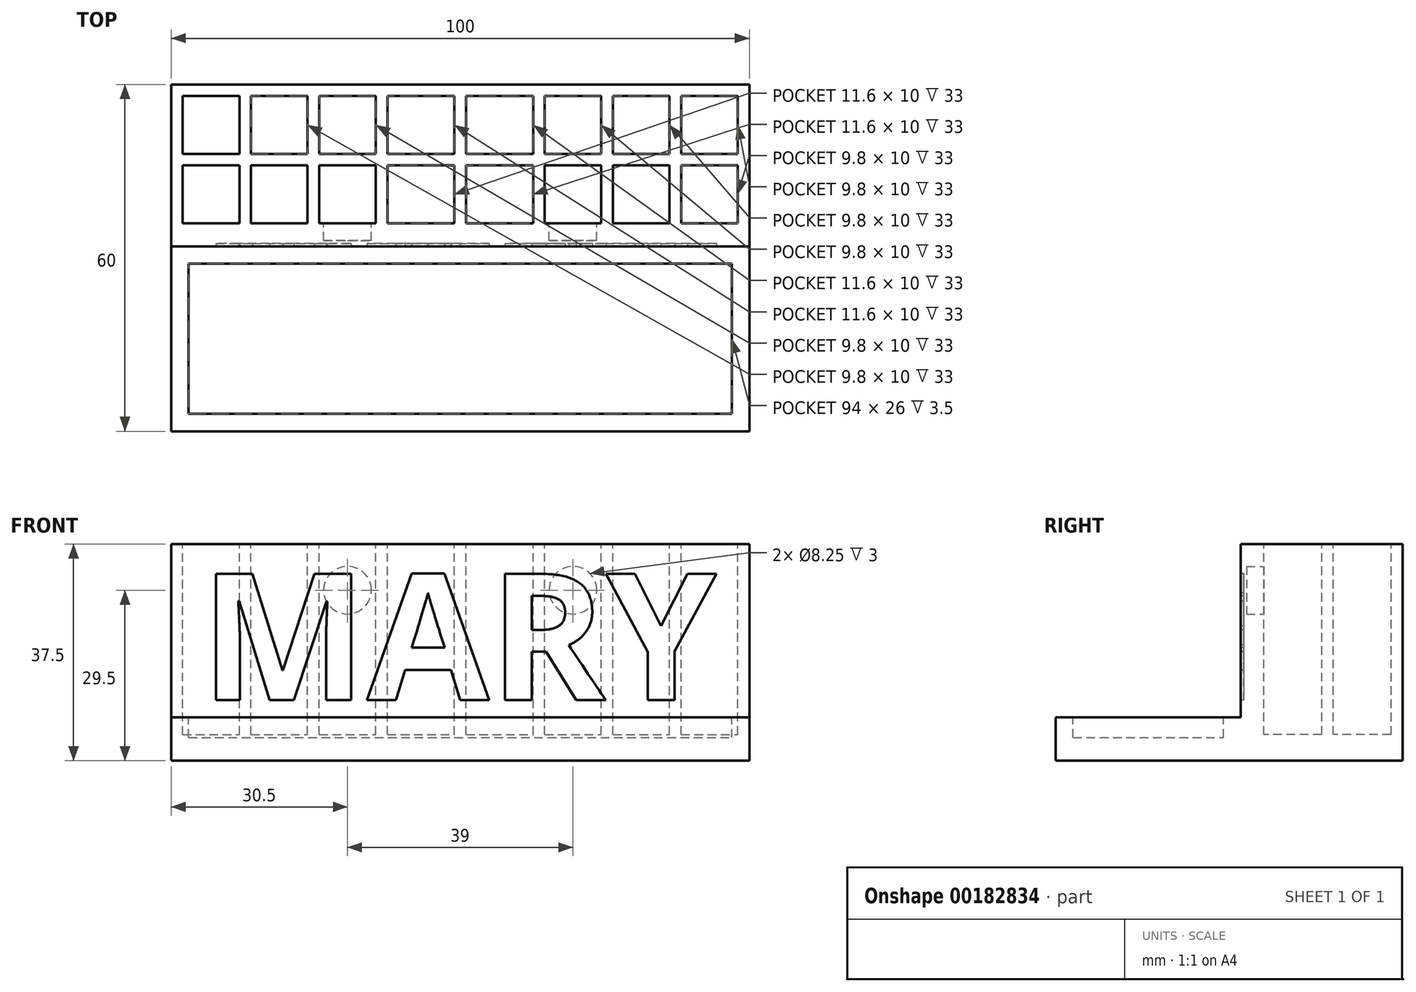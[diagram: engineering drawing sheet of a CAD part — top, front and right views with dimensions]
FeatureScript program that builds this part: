
annotation { "Feature Type Name" : "Feature", "Feature Type Description" : "" }
export const myFeature = defineFeature(function(context is Context, id is Id, definition is map)
    precondition{}
    {
        {
            var Q0;
            Q0=qCreatedBy(makeId("Top.planeOp"),FACE);
            var sketch = newSketch(context, id + "F0", { "sketchPlane" : qUnion([Q0])});
            skLineSegment(sketch, "E0.bottom", {"start": v(-50, 30) * mm, "end": v(50, 30) * mm});
            skLineSegment(sketch, "E0.top", {"start": v(-50, -30) * mm, "end": v(50, -30) * mm});
            skLineSegment(sketch, "E0.left", {"start": v(-50, 30) * mm, "end": v(-50, -30) * mm});
            skLineSegment(sketch, "E0.right", {"start": v(50, 30) * mm, "end": v(50, -30) * mm});
            skSolve(sketch);
        }
        {
            var Q0;
            Q0 = qSketchRegion(id + "F0", true);
            extrude(context, id + "F1", {"entities" : qUnion([Q0]), "depth" : 7.5 * mm});
        }
        {
            var Q0;
            Q0=makeQuery(id+"F1.opExtrude","CAP_FACE",FACE,{"disambiguationData":[OSD([sQuery(id+"F0.wireOp",EDGE,"E0.bottom"),sQuery(id+"F0.wireOp",EDGE,"E0.top"),sQuery(id+"F0.wireOp",EDGE,"E0.left"),sQuery(id+"F0.wireOp",EDGE,"E0.right")])],"isStart":false});
            var sketch = newSketch(context, id + "F2", { "sketchPlane" : qUnion([Q0])});
            skLineSegment(sketch, "E1.bottom", {"start": v(-50, 30) * mm, "end": v(50, 30) * mm});
            skLineSegment(sketch, "E1.top", {"start": v(-50, 2) * mm, "end": v(50, 2) * mm});
            skLineSegment(sketch, "E1.left", {"start": v(-50, 30) * mm, "end": v(-50, 2) * mm});
            skLineSegment(sketch, "E1.right", {"start": v(50, 30) * mm, "end": v(50, 2) * mm});
            skSolve(sketch);
        }
        {
            var Q0;
            Q0 = qSketchRegion(id + "F2", true);
            extrude(context, id + "F3", {"entities" : qUnion([Q0]), "operationType" : NewBodyOperationType.ADD, "depth" : 30 * mm});
        }
        {
            var Q0;
            Q0=makeQuery(id+"F3.opExtrude","CAP_FACE",FACE,{"disambiguationData":[OSD([sQuery(id+"F2.wireOp",EDGE,"E1.bottom"),sQuery(id+"F2.wireOp",EDGE,"E1.top"),sQuery(id+"F2.wireOp",EDGE,"E1.left"),sQuery(id+"F2.wireOp",EDGE,"E1.right")])],"isStart":false});
            var sketch = newSketch(context, id + "F4", { "sketchPlane" : qUnion([Q0])});
            skLineSegment(sketch, "E2.bottom", {"start": v(-48, 28) * mm, "end": v(48, 28) * mm});
            skLineSegment(sketch, "E2.top", {"start": v(-48, 6) * mm, "end": v(48, 6) * mm});
            skLineSegment(sketch, "E2.left", {"start": v(-48, 28) * mm, "end": v(-48, 6) * mm});
            skLineSegment(sketch, "E2.right", {"start": v(48, 28) * mm, "end": v(48, 6) * mm});
            skLineSegment(sketch, "E3.bottom", {"start": v(-48, 18) * mm, "end": v(48, 18) * mm});
            skLineSegment(sketch, "E3.top", {"start": v(-48, 16) * mm, "end": v(48, 16) * mm});
            skLineSegment(sketch, "E3.left", {"start": v(-48, 18) * mm, "end": v(-48, 16) * mm});
            skLineSegment(sketch, "E3.right", {"start": v(48, 18) * mm, "end": v(48, 16) * mm});
            skLineSegment(sketch, "E4.bottom", {"start": v(-38.2, 28) * mm, "end": v(-36.2, 28) * mm});
            skLineSegment(sketch, "E4.top", {"start": v(-38.2, 6) * mm, "end": v(-36.2, 6) * mm});
            skLineSegment(sketch, "E4.left", {"start": v(-38.2, 28) * mm, "end": v(-38.2, 6) * mm});
            skLineSegment(sketch, "E4.right", {"start": v(-36.2, 28) * mm, "end": v(-36.2, 6) * mm});
            skLineSegment(sketch, "E5.bottom", {"start": v(38.2, 28) * mm, "end": v(36.2, 28) * mm});
            skLineSegment(sketch, "E5.top", {"start": v(38.2, 6) * mm, "end": v(36.2, 6) * mm});
            skLineSegment(sketch, "E5.left", {"start": v(38.2, 28) * mm, "end": v(38.2, 6) * mm});
            skLineSegment(sketch, "E5.right", {"start": v(36.2, 28) * mm, "end": v(36.2, 6) * mm});
            skLineSegment(sketch, "E6.bottom", {"start": v(26.4, 28) * mm, "end": v(24.4, 28) * mm});
            skLineSegment(sketch, "E6.top", {"start": v(26.4, 6) * mm, "end": v(24.4, 6) * mm});
            skLineSegment(sketch, "E6.left", {"start": v(26.4, 28) * mm, "end": v(26.4, 6) * mm});
            skLineSegment(sketch, "E6.right", {"start": v(24.4, 28) * mm, "end": v(24.4, 6) * mm});
            skLineSegment(sketch, "E7.bottom", {"start": v(-26.4, 28) * mm, "end": v(-24.4, 28) * mm});
            skLineSegment(sketch, "E7.top", {"start": v(-26.4, 6) * mm, "end": v(-24.4, 6) * mm});
            skLineSegment(sketch, "E7.left", {"start": v(-26.4, 28) * mm, "end": v(-26.4, 6) * mm});
            skLineSegment(sketch, "E7.right", {"start": v(-24.4, 28) * mm, "end": v(-24.4, 6) * mm});
            skLineSegment(sketch, "E8.bottom", {"start": v(14.6, 28) * mm, "end": v(12.6, 28) * mm});
            skLineSegment(sketch, "E8.top", {"start": v(14.6, 6) * mm, "end": v(12.6, 6) * mm});
            skLineSegment(sketch, "E8.left", {"start": v(14.6, 28) * mm, "end": v(14.6, 6) * mm});
            skLineSegment(sketch, "E8.right", {"start": v(12.6, 28) * mm, "end": v(12.6, 6) * mm});
            skLineSegment(sketch, "E9.bottom", {"start": v(-14.6, 28) * mm, "end": v(-12.6, 28) * mm});
            skLineSegment(sketch, "E9.top", {"start": v(-14.6, 6) * mm, "end": v(-12.6, 6) * mm});
            skLineSegment(sketch, "E9.left", {"start": v(-14.6, 28) * mm, "end": v(-14.6, 6) * mm});
            skLineSegment(sketch, "E9.right", {"start": v(-12.6, 28) * mm, "end": v(-12.6, 6) * mm});
            skLineSegment(sketch, "E10.bottom", {"start": v(-1, 28) * mm, "end": v(1, 28) * mm});
            skLineSegment(sketch, "E10.top", {"start": v(-1, 6) * mm, "end": v(1, 6) * mm});
            skLineSegment(sketch, "E10.left", {"start": v(-1, 28) * mm, "end": v(-1, 6) * mm});
            skLineSegment(sketch, "E10.right", {"start": v(1, 28) * mm, "end": v(1, 6) * mm});
            skSolve(sketch);
        }
        {
            var Q0;
            {var subQ0=sQuery(id+"F4.wireOp",EDGE,"E2.left");var subQ1=sQuery(id+"F4.wireOp",EDGE,"E2.bottom");var subQ2=makeQuery(id+"F4.imprint","INTERSECT",VERTEX,{"derivedFrom":[subQ1,subQ0]});Q0=makeQuery(id+"F4.imprint","IMPRINT",FACE,{"disambiguationData":[TD([[makeQuery(id+"F4.imprint","IMPRINT",EDGE,{"disambiguationData":[TD([[subQ2,-1.0]])],"derivedFrom":subQ1}),-1.0]])]});}
            var Q1;
            {var subQ0=sQuery(id+"F4.wireOp",EDGE,"E4.right");var subQ5=sQuery(id+"F4.wireOp",EDGE,"E3.bottom");var subQ6=makeQuery(id+"F4.imprint","INTERSECT",VERTEX,{"derivedFrom":[subQ5,subQ0]});Q1=makeQuery(id+"F4.imprint","IMPRINT",FACE,{"disambiguationData":[TD([[makeQuery(id+"F4.imprint","IMPRINT",EDGE,{"disambiguationData":[TD([[subQ6,-1.0]])],"derivedFrom":subQ5}),1.0]])]});}
            var Q2;
            {var subQ0=sQuery(id+"F4.wireOp",EDGE,"E7.right");var subQ5=sQuery(id+"F4.wireOp",EDGE,"E3.bottom");var subQ6=makeQuery(id+"F4.imprint","INTERSECT",VERTEX,{"derivedFrom":[subQ5,subQ0]});Q2=makeQuery(id+"F4.imprint","IMPRINT",FACE,{"disambiguationData":[TD([[makeQuery(id+"F4.imprint","IMPRINT",EDGE,{"disambiguationData":[TD([[subQ6,-1.0]])],"derivedFrom":subQ5}),1.0]])]});}
            var Q3;
            {var subQ0=sQuery(id+"F4.wireOp",EDGE,"E9.right");var subQ5=sQuery(id+"F4.wireOp",EDGE,"E3.bottom");var subQ6=makeQuery(id+"F4.imprint","INTERSECT",VERTEX,{"derivedFrom":[subQ5,subQ0]});Q3=makeQuery(id+"F4.imprint","IMPRINT",FACE,{"disambiguationData":[TD([[makeQuery(id+"F4.imprint","IMPRINT",EDGE,{"disambiguationData":[TD([[subQ6,-1.0]])],"derivedFrom":subQ5}),1.0]])]});}
            var Q4;
            {var subQ3=sQuery(id+"F4.wireOp",EDGE,"E10.right");var subQ5=sQuery(id+"F4.wireOp",EDGE,"E3.bottom");var subQ6=makeQuery(id+"F4.imprint","INTERSECT",VERTEX,{"derivedFrom":[subQ5,subQ3]});Q4=makeQuery(id+"F4.imprint","IMPRINT",FACE,{"disambiguationData":[TD([[makeQuery(id+"F4.imprint","IMPRINT",EDGE,{"disambiguationData":[TD([[subQ6,-1.0]])],"derivedFrom":subQ5}),1.0]])]});}
            var Q5;
            {var subQ3=sQuery(id+"F4.wireOp",EDGE,"E8.left");var subQ5=sQuery(id+"F4.wireOp",EDGE,"E3.bottom");var subQ6=makeQuery(id+"F4.imprint","INTERSECT",VERTEX,{"derivedFrom":[subQ5,subQ3]});Q5=makeQuery(id+"F4.imprint","IMPRINT",FACE,{"disambiguationData":[TD([[makeQuery(id+"F4.imprint","IMPRINT",EDGE,{"disambiguationData":[TD([[subQ6,-1.0]])],"derivedFrom":subQ5}),1.0]])]});}
            var Q6;
            {var subQ3=sQuery(id+"F4.wireOp",EDGE,"E6.left");var subQ5=sQuery(id+"F4.wireOp",EDGE,"E3.bottom");var subQ6=makeQuery(id+"F4.imprint","INTERSECT",VERTEX,{"derivedFrom":[subQ5,subQ3]});Q6=makeQuery(id+"F4.imprint","IMPRINT",FACE,{"disambiguationData":[TD([[makeQuery(id+"F4.imprint","IMPRINT",EDGE,{"disambiguationData":[TD([[subQ6,-1.0]])],"derivedFrom":subQ5}),1.0]])]});}
            var Q7;
            {var subQ0=sQuery(id+"F4.wireOp",EDGE,"E2.right");var subQ1=sQuery(id+"F4.wireOp",EDGE,"E2.bottom");var subQ2=makeQuery(id+"F4.imprint","INTERSECT",VERTEX,{"derivedFrom":[subQ1,subQ0]});Q7=makeQuery(id+"F4.imprint","IMPRINT",FACE,{"disambiguationData":[TD([[makeQuery(id+"F4.imprint","IMPRINT",EDGE,{"disambiguationData":[TD([[subQ2,1.0]])],"derivedFrom":subQ1}),-1.0]])]});}
            var Q8;
            {var subQ0=sQuery(id+"F4.wireOp",EDGE,"E2.right");var subQ1=sQuery(id+"F4.wireOp",EDGE,"E2.top");var subQ2=makeQuery(id+"F4.imprint","INTERSECT",VERTEX,{"derivedFrom":[subQ1,subQ0]});Q8=makeQuery(id+"F4.imprint","IMPRINT",FACE,{"disambiguationData":[TD([[makeQuery(id+"F4.imprint","IMPRINT",EDGE,{"disambiguationData":[TD([[subQ2,1.0]])],"derivedFrom":subQ1}),1.0]])]});}
            var Q9;
            {var subQ3=sQuery(id+"F4.wireOp",EDGE,"E6.left");var subQ5=sQuery(id+"F4.wireOp",EDGE,"E3.top");var subQ6=makeQuery(id+"F4.imprint","INTERSECT",VERTEX,{"derivedFrom":[subQ5,subQ3]});Q9=makeQuery(id+"F4.imprint","IMPRINT",FACE,{"disambiguationData":[TD([[makeQuery(id+"F4.imprint","IMPRINT",EDGE,{"disambiguationData":[TD([[subQ6,-1.0]])],"derivedFrom":subQ5}),-1.0]])]});}
            var Q10;
            {var subQ3=sQuery(id+"F4.wireOp",EDGE,"E8.left");var subQ5=sQuery(id+"F4.wireOp",EDGE,"E3.top");var subQ6=makeQuery(id+"F4.imprint","INTERSECT",VERTEX,{"derivedFrom":[subQ5,subQ3]});Q10=makeQuery(id+"F4.imprint","IMPRINT",FACE,{"disambiguationData":[TD([[makeQuery(id+"F4.imprint","IMPRINT",EDGE,{"disambiguationData":[TD([[subQ6,-1.0]])],"derivedFrom":subQ5}),-1.0]])]});}
            var Q11;
            {var subQ3=sQuery(id+"F4.wireOp",EDGE,"E10.right");var subQ5=sQuery(id+"F4.wireOp",EDGE,"E3.top");var subQ7=makeQuery(id+"F4.imprint","INTERSECT",VERTEX,{"derivedFrom":[subQ5,subQ3]});Q11=makeQuery(id+"F4.imprint","IMPRINT",FACE,{"disambiguationData":[TD([[makeQuery(id+"F4.imprint","IMPRINT",EDGE,{"disambiguationData":[TD([[subQ7,-1.0]])],"derivedFrom":subQ5}),-1.0]])]});}
            var Q12;
            {var subQ0=sQuery(id+"F4.wireOp",EDGE,"E9.right");var subQ5=sQuery(id+"F4.wireOp",EDGE,"E3.top");var subQ6=makeQuery(id+"F4.imprint","INTERSECT",VERTEX,{"derivedFrom":[subQ5,subQ0]});Q12=makeQuery(id+"F4.imprint","IMPRINT",FACE,{"disambiguationData":[TD([[makeQuery(id+"F4.imprint","IMPRINT",EDGE,{"disambiguationData":[TD([[subQ6,-1.0]])],"derivedFrom":subQ5}),-1.0]])]});}
            var Q13;
            {var subQ0=sQuery(id+"F4.wireOp",EDGE,"E7.right");var subQ5=sQuery(id+"F4.wireOp",EDGE,"E3.top");var subQ6=makeQuery(id+"F4.imprint","INTERSECT",VERTEX,{"derivedFrom":[subQ5,subQ0]});Q13=makeQuery(id+"F4.imprint","IMPRINT",FACE,{"disambiguationData":[TD([[makeQuery(id+"F4.imprint","IMPRINT",EDGE,{"disambiguationData":[TD([[subQ6,-1.0]])],"derivedFrom":subQ5}),-1.0]])]});}
            var Q14;
            {var subQ0=sQuery(id+"F4.wireOp",EDGE,"E4.right");var subQ5=sQuery(id+"F4.wireOp",EDGE,"E3.top");var subQ6=makeQuery(id+"F4.imprint","INTERSECT",VERTEX,{"derivedFrom":[subQ5,subQ0]});Q14=makeQuery(id+"F4.imprint","IMPRINT",FACE,{"disambiguationData":[TD([[makeQuery(id+"F4.imprint","IMPRINT",EDGE,{"disambiguationData":[TD([[subQ6,-1.0]])],"derivedFrom":subQ5}),-1.0]])]});}
            var Q15;
            {var subQ0=sQuery(id+"F4.wireOp",EDGE,"E2.left");var subQ1=sQuery(id+"F4.wireOp",EDGE,"E2.top");var subQ2=makeQuery(id+"F4.imprint","INTERSECT",VERTEX,{"derivedFrom":[subQ1,subQ0]});Q15=makeQuery(id+"F4.imprint","IMPRINT",FACE,{"disambiguationData":[TD([[makeQuery(id+"F4.imprint","IMPRINT",EDGE,{"disambiguationData":[TD([[subQ2,-1.0]])],"derivedFrom":subQ1}),1.0]])]});}
            extrude(context, id + "F5", {"entities" : qUnion([Q0, Q1, Q2, Q3, Q4, Q5, Q6, Q7, Q8, Q9, Q10, Q11, Q12, Q13, Q14, Q15]), "operationType" : NewBodyOperationType.REMOVE, "oppositeDirection" : true, "depth" : 33 * mm});
        }
        {
            var Q0;
            Q0=makeQuery(id+"F1.opExtrude","CAP_FACE",FACE,{"disambiguationData":[OSD([sQuery(id+"F0.wireOp",EDGE,"E0.bottom"),sQuery(id+"F0.wireOp",EDGE,"E0.top"),sQuery(id+"F0.wireOp",EDGE,"E0.left"),sQuery(id+"F0.wireOp",EDGE,"E0.right")])],"isStart":false});
            var sketch = newSketch(context, id + "F6", { "sketchPlane" : qUnion([Q0])});
            skLineSegment(sketch, "E11.bottom", {"start": v(-47, -27) * mm, "end": v(47, -27) * mm});
            skLineSegment(sketch, "E11.top", {"start": v(-47, -1) * mm, "end": v(47, -1) * mm});
            skLineSegment(sketch, "E11.left", {"start": v(-47, -27) * mm, "end": v(-47, -1) * mm});
            skLineSegment(sketch, "E11.right", {"start": v(47, -27) * mm, "end": v(47, -1) * mm});
            skSolve(sketch);
        }
        {
            var Q0;
            Q0 = qSketchRegion(id + "F6", true);
            extrude(context, id + "F7", {"entities" : qUnion([Q0]), "operationType" : NewBodyOperationType.REMOVE, "oppositeDirection" : true, "depth" : 3.5 * mm});
        }
        {
            var Q0;
            Q0=makeQuery(id+"F3.opExtrude","SWEPT_FACE",FACE,{"disambiguationData":[OSD([sQuery(id+"F2.wireOp",EDGE,"E1.top")])]});
            var sketch = newSketch(context, id + "F8", { "sketchPlane" : qUnion([Q0])});
            skText(sketch, "E12", { "text": "MARY", "fontName": "OpenSans-Bold.ttf"});
            const initialGuessF8  = {"E12": [-0.045, 0.01046, 1, 0, 0.02204]};
            skSetInitialGuess(sketch, initialGuessF8);
            skSolve(sketch);
        }
        {
            var Q0;
            Q0=makeQuery(id+"F8.imprint","IMPRINT",FACE,{"disambiguationData":[TD([[makeQuery(id+"F8.imprint","IMPRINT",EDGE,{"derivedFrom":sQuery(id+"F8.wireOp",EDGE,"E12.sketch_text.stroke-0")}),-1.0]])]});
            var Q1;
            Q1=makeQuery(id+"F8.imprint","IMPRINT",FACE,{"disambiguationData":[TD([[makeQuery(id+"F8.imprint","IMPRINT",EDGE,{"derivedFrom":sQuery(id+"F8.wireOp",EDGE,"E12.sketch_text.stroke-19")}),-1.0]])]});
            var Q2;
            Q2=makeQuery(id+"F8.imprint","IMPRINT",FACE,{"disambiguationData":[TD([[makeQuery(id+"F8.imprint","IMPRINT",EDGE,{"derivedFrom":sQuery(id+"F8.wireOp",EDGE,"E12.sketch_text.stroke-31")}),-1.0]])]});
            var Q3;
            Q3=makeQuery(id+"F8.imprint","IMPRINT",FACE,{"disambiguationData":[TD([[makeQuery(id+"F8.imprint","IMPRINT",EDGE,{"derivedFrom":sQuery(id+"F8.wireOp",EDGE,"E12.sketch_text.stroke-50")}),-1.0]])]});
            extrude(context, id + "F9", {"entities" : qUnion([Q0, Q1, Q2, Q3]), "operationType" : NewBodyOperationType.REMOVE, "oppositeDirection" : true, "depth" : .5 * mm});
        }
        {
            var Q0;
            {var subQ0=sQuery(id+"F4.wireOp",EDGE,"E2.top");Q0=makeQuery(id+"F5.boolean.opBoolean","COPY",FACE,{"derivedFrom":makeQuery(id+"F5.opExtrude","SWEPT_FACE",FACE,{"disambiguationData":[OSD([subQ0]),TDD([makeQuery(id+"F4.imprint","IMPRINT",EDGE,{"disambiguationData":[TD([[makeQuery(id+"F4.imprint","INTERSECT",VERTEX,{"derivedFrom":[subQ0,sQuery(id+"F4.wireOp",EDGE,"E6.top"),sQuery(id+"F4.wireOp",EDGE,"E6.right")]}),1.0]])],"derivedFrom":subQ0})])]})});}
            var sketch = newSketch(context, id + "F10", { "sketchPlane" : qUnion([Q0])});
            skCircle(sketch, "E13", {"center": v(-19.5, 29.5) * mm, "radius": 4.12 * mm});
            skSolve(sketch);
        }
        {
            var Q0;
            Q0 = qSketchRegion(id + "F10", true);
            extrude(context, id + "F11", {"entities" : qUnion([Q0]), "operationType" : NewBodyOperationType.REMOVE, "oppositeDirection" : true, "depth" : 3 * mm});
        }
        {
            var Q0;
            {var subQ0=sQuery(id+"F4.wireOp",EDGE,"E2.top");Q0=makeQuery(id+"F5.boolean.opBoolean","COPY",FACE,{"derivedFrom":makeQuery(id+"F5.opExtrude","SWEPT_FACE",FACE,{"disambiguationData":[OSD([subQ0]),TDD([makeQuery(id+"F4.imprint","IMPRINT",EDGE,{"disambiguationData":[TD([[makeQuery(id+"F4.imprint","INTERSECT",VERTEX,{"derivedFrom":[subQ0,sQuery(id+"F4.wireOp",EDGE,"E7.top"),sQuery(id+"F4.wireOp",EDGE,"E7.right")]}),-1.0]])],"derivedFrom":subQ0})])]})});}
            var sketch = newSketch(context, id + "F12", { "sketchPlane" : qUnion([Q0])});
            skCircle(sketch, "E14", {"center": v(19.5, 29.5) * mm, "radius": 4.12 * mm});
            skPoint(sketch, "E14.centerSnap0", {"position": v(19.5, 37.5) * mm});
            skSolve(sketch);
        }
        {
            var Q0;
            Q0 = qSketchRegion(id + "F12", true);
            extrude(context, id + "F13", {"entities" : qUnion([Q0]), "operationType" : NewBodyOperationType.REMOVE, "oppositeDirection" : true, "depth" : 3 * mm});
        }
    });
